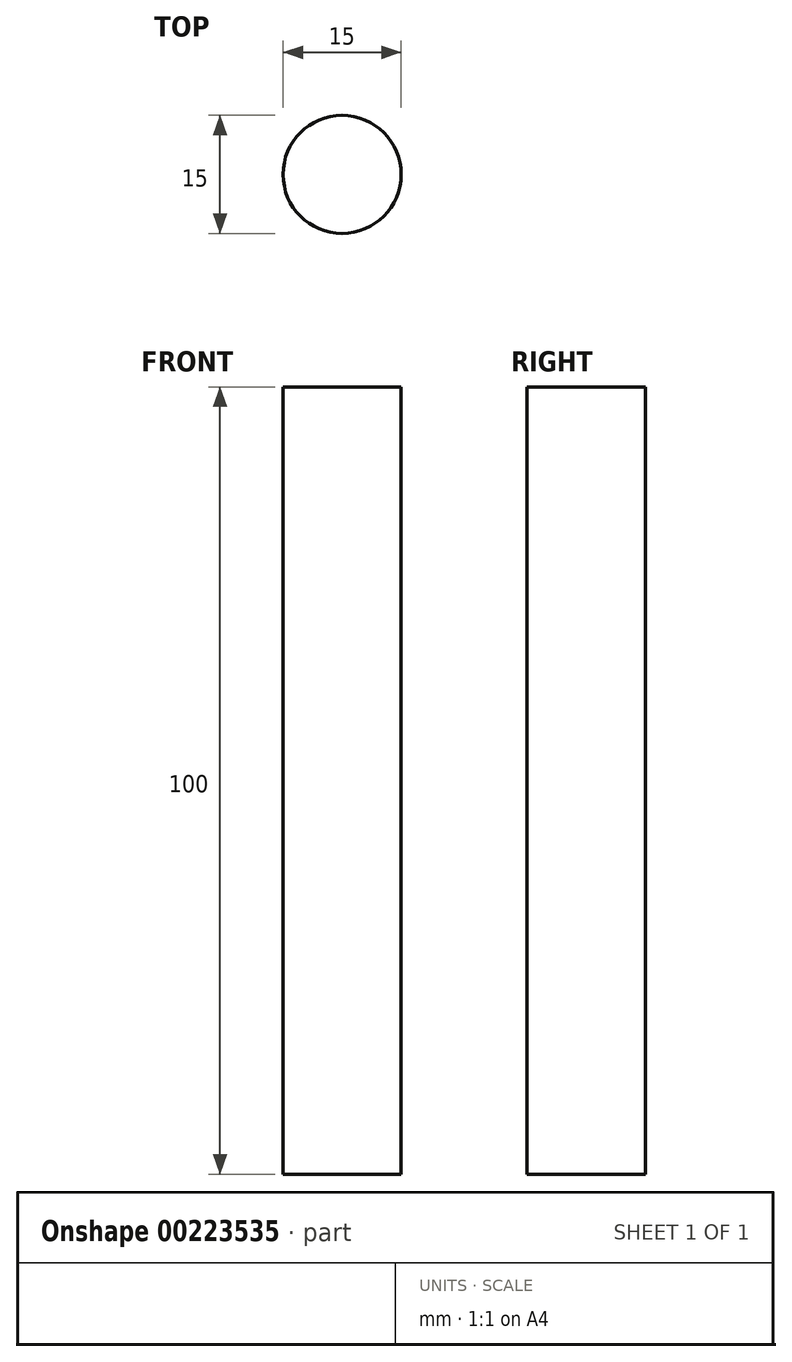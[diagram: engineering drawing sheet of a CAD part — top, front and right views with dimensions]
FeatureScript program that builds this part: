
annotation { "Feature Type Name" : "Feature", "Feature Type Description" : "" }
export const myFeature = defineFeature(function(context is Context, id is Id, definition is map)
    precondition{}
    {
        {
            var Q0;
            Q0=qCreatedBy(makeId("Top.planeOp"),FACE);
            var sketch = newSketch(context, id + "F0", { "sketchPlane" : qUnion([Q0])});
            skCircle(sketch, "E0", {"center": v(0, 0) * mm, "radius": 7.5 * mm});
            skSolve(sketch);
        }
        {
            var Q0;
            Q0=qSketchRegion(id+"F0",true);
            extrude(context, id + "F1", {"entities" : qUnion([Q0]), "depth" : 100 * mm});
        }
    });
